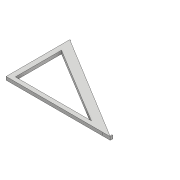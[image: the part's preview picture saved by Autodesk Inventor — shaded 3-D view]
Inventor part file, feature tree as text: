
AUTODESK INVENTOR PART (.ipt)
format: ipt  version: 2017 (Build 210142000, 142)  size: 129,024 bytes
history: native  units: mm
features: extrude x7, sketch x7
ambient origin geometry x8: Origin, YZ Plane, XZ Plane, XY Plane, X Axis, Y Axis, Z Axis, Center Point
bodies: Solid1 (feature_tree)
feature tree (14):
  extrude  "Extrusion1"  Depth=365.0mm
  extrude  "Extrusion2"  Depth=20.0mm TaperAngle=0.0deg
  extrude  "Extrusion3"  Depth=4.0mm TaperAngle=0.0deg
  extrude  "Extrusion4"  Depth=15.0mm
  extrude  "Extrusion5"  Depth=5.0mm TaperAngle=0.0deg
  extrude  "Extrusion6"  [1 undecoded]
  extrude  "Extrusion7"  [1 undecoded]
  sketch  "Sketch1"  dims[d0=365.0mm d1=700.0mm]
  sketch  "Sketch2"  dims[d2=20.0mm d3=0.0mm d4=161.75mm d5=0.0mm]
  sketch  "Sketch3"  dims[d6=4.0mm d7=0.0mm d8=4.0mm d9=0.0mm]
  sketch  "Sketch4"  dims[d10=2.75mm d11=0.0mm d12=15.0mm]
  sketch  "Sketch5"  dims[d13=5.0mm d14=0.0mm d15=5.0mm d16=0.0mm]
  sketch  "Sketch6"
  sketch  "Sketch7"
note: 2 required parameter values undecoded (feature->parameter linkage not recoverable at this tier; creation-order binding heuristic only, values carry confidence <= 0.55)
